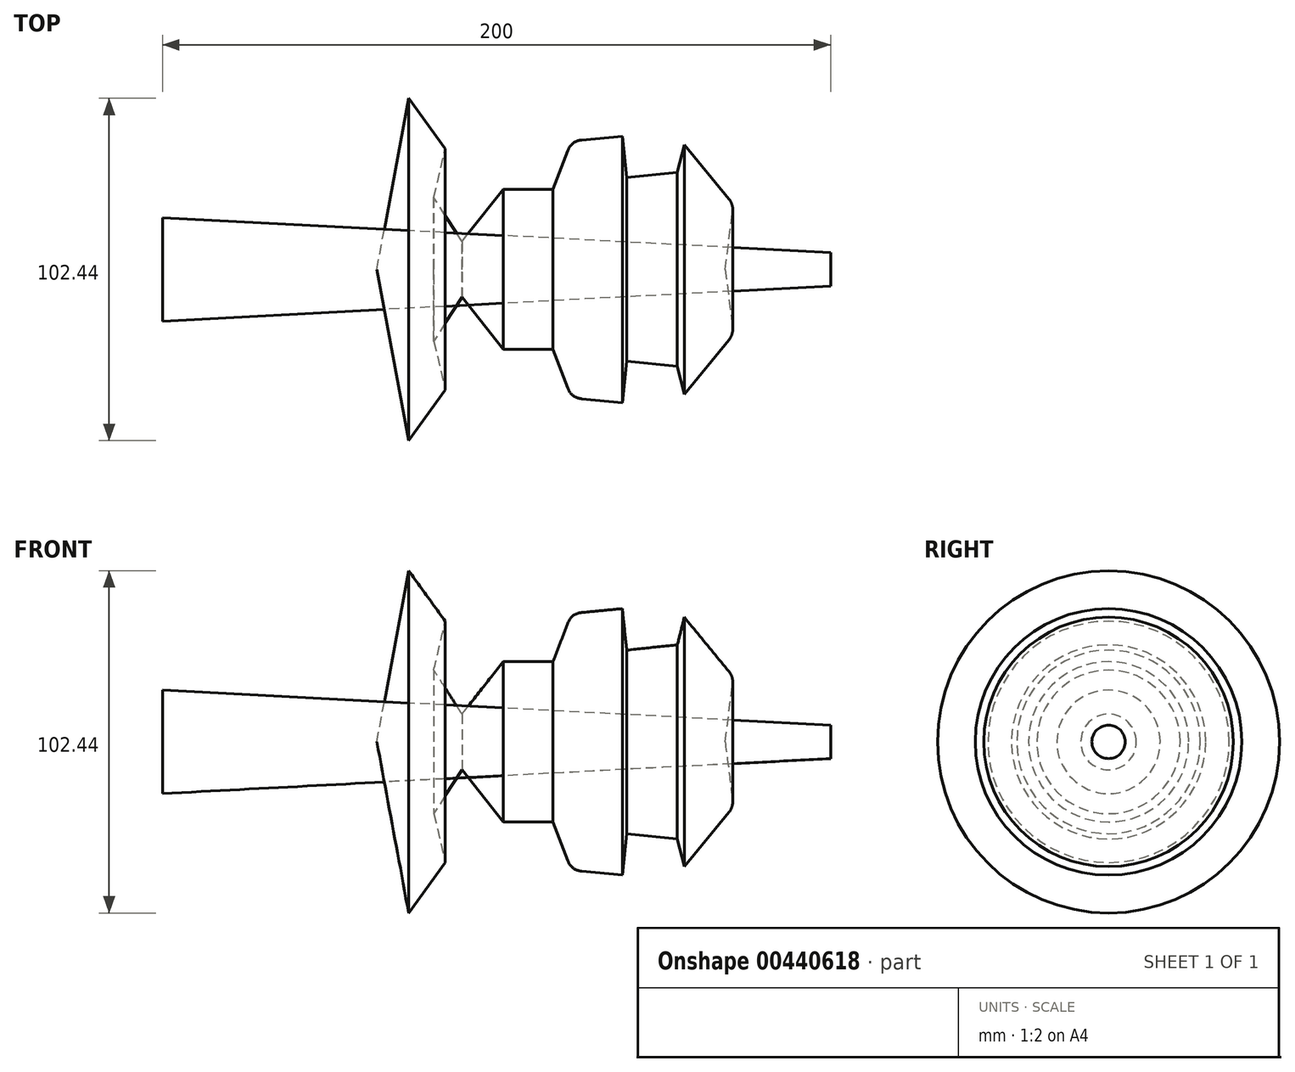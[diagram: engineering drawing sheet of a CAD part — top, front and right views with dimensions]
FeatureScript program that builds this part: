
annotation { "Feature Type Name" : "Feature", "Feature Type Description" : "" }
export const myFeature = defineFeature(function(context is Context, id is Id, definition is map)
    precondition{}
    {
        {
            var Q0;
            Q0=qCreatedBy(makeId("Top.planeOp"),FACE);
            var sketch = newSketch(context, id + "F0", { "sketchPlane" : qUnion([Q0])});
            skLineSegment(sketch, "E0", {"start": v(-7.16, 23.98) * mm, "end": v(7.78, 23.98) * mm});
            skLineSegment(sketch, "E1", {"start": v(7.78, 23.98) * mm, "end": v(13.32, 38.44) * mm});
            skLineSegment(sketch, "E2", {"start": v(13.32, 38.44) * mm, "end": v(28.53, 39.88) * mm});
            skLineSegment(sketch, "E3", {"start": v(28.53, 39.88) * mm, "end": v(29.84, 27.46) * mm});
            skLineSegment(sketch, "E4", {"start": v(29.84, 27.46) * mm, "end": v(45.02, 29.07) * mm});
            skLineSegment(sketch, "E5", {"start": v(45.02, 29.07) * mm, "end": v(47.09, 37.33) * mm});
            skLineSegment(sketch, "E6", {"start": v(47.09, 37.33) * mm, "end": v(61.81, 19.4) * mm});
            skLineSegment(sketch, "E7", {"start": v(61.81, 19.4) * mm, "end": v(59.3, 0) * mm});
            skLineSegment(sketch, "E8", {"start": v(59.3, 0) * mm, "end": v(-44.95, 0) * mm});
            skLineSegment(sketch, "E9", {"start": v(-44.95, 0) * mm, "end": v(-35.42, 51.22) * mm});
            skLineSegment(sketch, "E10", {"start": v(-35.42, 51.22) * mm, "end": v(-24.44, 36.1) * mm});
            skLineSegment(sketch, "E11", {"start": v(-24.44, 36.1) * mm, "end": v(-27.9, 21.49) * mm});
            skLineSegment(sketch, "E12", {"start": v(-27.9, 21.49) * mm, "end": v(-19.48, 8.33) * mm});
            skLineSegment(sketch, "E13", {"start": v(-19.48, 8.33) * mm, "end": v(-7.16, 23.98) * mm});
            skLineSegment(sketch, "E14", {"start": v(-64.95, 0) * mm, "end": v(90.88, 0) * mm, "construction": true});
            skSolve(sketch);
        }
        {
            var Q0;
            Q0=qSketchRegion(id+"F0",true);
            var Q1;
            Q1=sQuery(id+"F0.wireOp",EDGE,"E14");
            revolve(context, id + "F1", {"entities" : qUnion([Q0]), "axis" : qUnion([Q1]), "revolveType" : RevolveType.FULL});
        }
        {
            var Q0;
            Q0=makeQuery(id+"F1.opRevolve","SWEPT_EDGE",EDGE,{"disambiguationData":[OSD([sQuery(id+"F0.wireOp",EDGE,"E6"),sQuery(id+"F0.wireOp",EDGE,"E7")])]});
            var Q1;
            Q1=makeQuery(id+"F1.opRevolve","SWEPT_EDGE",EDGE,{"disambiguationData":[OSD([sQuery(id+"F0.wireOp",EDGE,"E1"),sQuery(id+"F0.wireOp",EDGE,"E2")])]});
            fillet(context, id + "F2", {"entities" : qUnion([Q0, Q1]), "radius" : 5 * mm, "rho" : 0.5, "crossSection" : FilletCrossSection.CONIC, "allowEdgeOverflow" : false});
        }
        {
            var Q0;
            Q0=qCreatedBy(makeId("Right.planeOp"),FACE);
            var Q1;
            Q1=sQuery(id+"F0.wireOp",VERTEX,"E14.end");
            cPlane(context, id + "F3", {"entities" : qUnion([Q0, Q1]), "cplaneType" : CPlaneType.PLANE_POINT, "offset" : 67.83 * mm, "width" : 150 * mm, "height" : 150 * mm});
        }
        {
            var Q0;
            Q0=qCreatedBy(id+"F3.planeOp",FACE);
            var sketch = newSketch(context, id + "F4", { "sketchPlane" : qUnion([Q0])});
            skCircle(sketch, "E15", {"center": v(0, 0) * mm, "radius": 5 * mm});
            skSolve(sketch);
        }
        {
            var Q0;
            Q0=makeQuery(id+"F4.imprint","IMPRINT",FACE,{"disambiguationData":[TD([[makeQuery(id+"F4.imprint","IMPRINT",EDGE,{"derivedFrom":sQuery(id+"F4.wireOp",EDGE,"E15")}),1.0]])]});
            extrude(context, id + "F5", {"entities" : qUnion([Q0]), "oppositeDirection" : true, "depth" : 200 * mm, "hasDraft" : true, "draftAngle" : 3 * degree});
        }
    });
